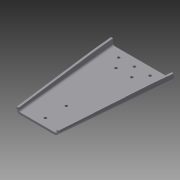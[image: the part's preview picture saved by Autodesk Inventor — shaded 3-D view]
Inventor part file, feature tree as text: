
AUTODESK INVENTOR PART (.ipt)
format: ipt  version: 2013 (Build 170138000, 138)  size: 206,336 bytes
history: native  units: in
note: dims shown in document units (in); Inventor stores cm internally (conversion verified against a paired STEP export)
features: sheet_metal_op x4, sketch x3, other x3, chamfer x1, mirror x1, hole x1
ambient origin geometry x8: Origin, YZ Plane, XZ Plane, XY Plane, X Axis, Y Axis, Z Axis, Center Point
bodies: Solid1 (feature_tree)
feature tree (13):
  sheet_metal_op  "Face1"
  sheet_metal_op  "Flange1"
  chamfer  "Chamfer1"  Distance=0.1875in
  mirror  "Mirror1"
  hole  "Hole1"  [1 undecoded]
  sketch  "Sketch1"  dims[d0=3.0in]
  other  "Plate1"
  sketch  "Sketch2"  dims[d1=10.0in]
  other  "Plate2"
  sheet_metal_op  "Bend1"
  sheet_metal_op  "Corner1"
  sketch  "Sketch3"  dims[d2=1.0in d3=0.1875in d4=0.1875in d5=0.0938in d6=0.375in d7=0.1875in d8=0.75in d9=90.0deg d10=0.1875in d11=0.75in d12=0.1875in d13=0.1875in d14=8.0623in d15=0.25in d16=45.0deg d17=1.5in d19=1.5in d20=0.75in d21=0.75in d24=1.0in d25=0.75in d26=0.25in d27=0.75in d28=0.375in d29=0.25in d30=0.5635in d31=0.1875in d32=0.8108in d33=0.75in d34=2.0in d35=3.0in]
  other  "Definition1"
note: 1 required parameter value undecoded (feature->parameter linkage not recoverable at this tier; creation-order binding heuristic only, values carry confidence <= 0.55)
